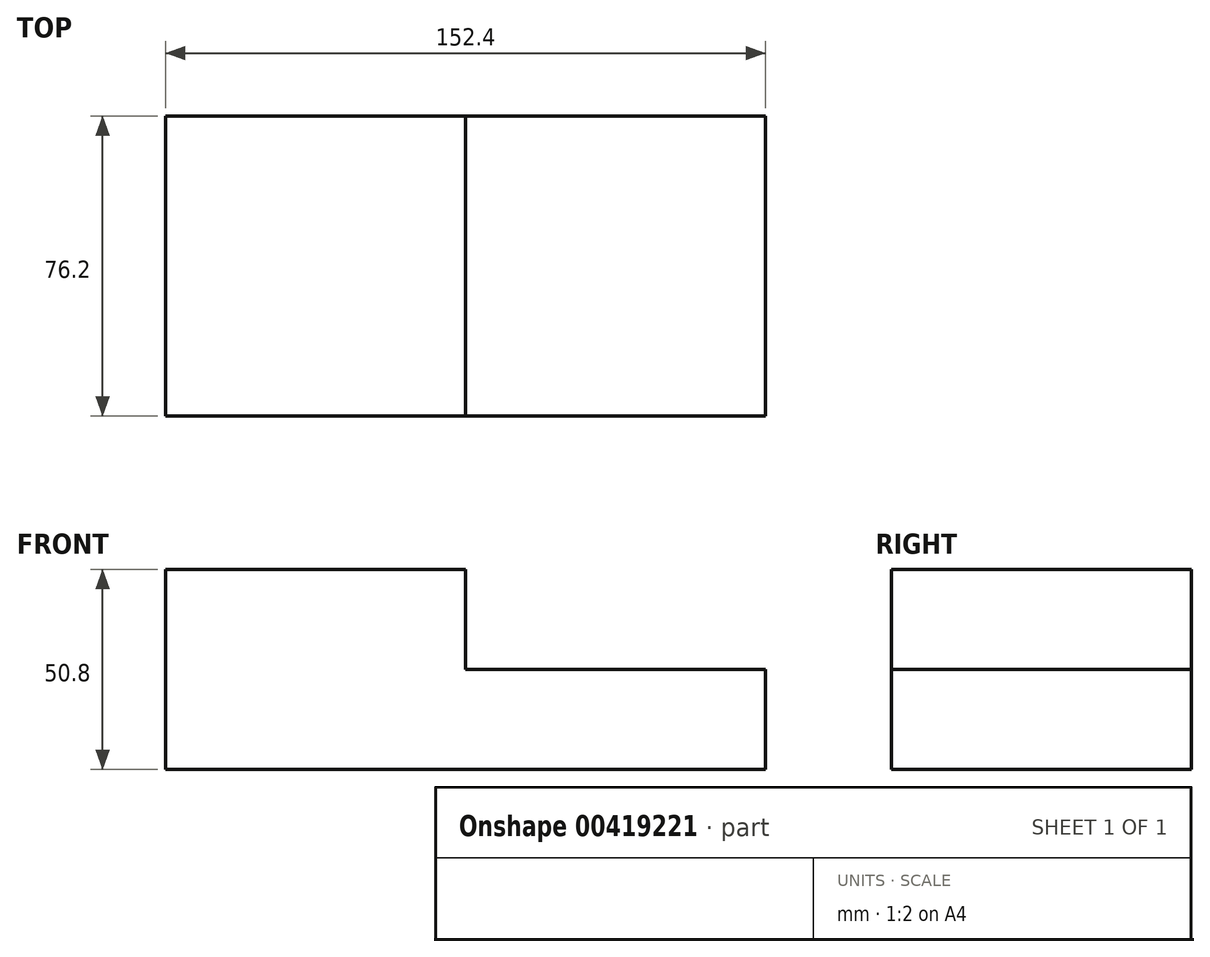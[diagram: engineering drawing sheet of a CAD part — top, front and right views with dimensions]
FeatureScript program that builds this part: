
annotation { "Feature Type Name" : "Feature", "Feature Type Description" : "" }
export const myFeature = defineFeature(function(context is Context, id is Id, definition is map)
    precondition{}
    {
        {
            var Q0;
            Q0=qCreatedBy(makeId("Front.planeOp"),FACE);
            var sketch = newSketch(context, id + "F0", { "sketchPlane" : qUnion([Q0])});
            skLineSegment(sketch, "E0", {"start": v(0, 0) * mm, "end": v(152.4, 0) * mm});
            skLineSegment(sketch, "E1", {"start": v(152.4, 0) * mm, "end": v(152.4, 25.4) * mm});
            skLineSegment(sketch, "E2", {"start": v(152.4, 25.4) * mm, "end": v(76.2, 25.4) * mm});
            skLineSegment(sketch, "E3", {"start": v(76.2, 25.4) * mm, "end": v(76.2, 50.8) * mm});
            skLineSegment(sketch, "E4", {"start": v(76.2, 50.8) * mm, "end": v(0, 50.8) * mm});
            skLineSegment(sketch, "E5", {"start": v(0, 50.8) * mm, "end": v(0, 0) * mm});
            skSolve(sketch);
        }
        {
            var Q0;
            Q0 = qSketchRegion(id + "F0", true);
            extrude(context, id + "F1", {"entities" : qUnion([Q0]), "depth" : 76.2 * mm});
        }
    });
